# Revit family: SOT_Mavone_Multiproduct_BIM_GB_T0045;T0046;T0047;T0048
name_source: partatom
category: Plumbing Fixtures
revit_build: Autodesk Revit MEP 2014 (Build: 20130308_1515(x64)
units: mm (PartAtom-declared; Revit-internal decimal feet)

## types (16) — shared parameters
Accessories = www.specifysottini.co.uk
AreaUnits = millimeters
Assembly Code = C1030200
AssetType = Fixed
BREEAM = No
Brand = Sottini
CodePerformance = EN 14749:2005
Default Elevation = 900 mm  [stored 2.95276 ft]
DurationUnit = year
ECA = No
ExpectedLife = 30
Finish = White
Handle = SOT_Sottini_Fittings_Chrome_Render
IfcExportAs = IfcFurnitureType
IfcExportType = USERDEFINED
InstallationInstructions = www.idealspec.co.uk/resources.html
LinearUnits = millimeters
MainColor = White
ManufacturerURL = www.specifysottini.co.uk
Material = Laminated board
NBSDescription = Bathroom integrated duct work
NBSReference = 45-35-72/320
NominalDepth = 360 mm
NominalHeight = 400 mm  [stored 1.31234 ft]
NominalLength = 400 mm  [stored 1.31234 ft]
Shape = Rectangular
Space = Internal
SpareParts = www.fastpart-spares.co.uk
SustainabilityPerformance = FSC
TMV3 = No
URL = www.specifysottini.co.uk
Uniclass2 = Pr_40_30_78_04
Version = 1
VolumeUnits = Litres
WRAS = No
WarrantyDescription = Manufacturers warranty
WarrantyDurationParts = 5
WarrantyDurationUnit = year
WaterEfficientProduct = No
zero-valued in all types: CWFU, Cost, HWFU, WFU

## per-type parameters (varying)
| type | BIMObjectName | Color | Description | Features | Laminate | Model | Name | NettWeight | NominalWidth | ProductInformation | Size |
| T0045OV - Mavone 500mm wall hung vanity unit - 1 drawer - Gloss White | SOT_Sottini_Furniture_Mavone_T0045OV | White | Mavone 50 cm wall hung vanity unit with 1 drawer and integrated handle | 50 cm wall hung vanity unit with 1 drawer and integrated handle | SOT_Sottini_Laminate_White_OV_Render | T0045OV | Furniture_Mavone_T0045OV_Sottini | 11 Kg | 500 mm  [stored 1.64042 ft] | www.idealspec.co.uk/assets/datasheet/T0045OV | 360 x 400 x 500 mm |
| T0046OV - Mavone 600mm wall hung vanity unit - 1 drawer - Gloss White | SOT_Sottini_Furniture_Mavone_T0046OV | White | Mavone 60 cm wall hung vanity unit with 1 drawer and integrated handle | 60 cm wall hung vanity unit with 1 drawer and integrated handle | SOT_Sottini_Laminate_White_OV_Render | T0046OV | Furniture_Mavone_T0046OV_Sottini | 14 Kg | 600 mm | www.idealspec.co.uk/assets/datasheet/T0046OV | 360 x 400 x 600 mm |
| T0047OV - Mavone 800mm wall hung vanity unit - 1 drawer - Gloss White | SOT_Sottini_Furniture_Mavone_T0047OV | White | Mavone 80 cm wall hung vanity unit with 1 drawer and integrated handle | 80 cm wall hung vanity unit with 1 drawer and integrated handle | SOT_Sottini_Laminate_White_OV_Render | T0047OV | Furniture_Mavone_T0047OV_Sottini | 18 Kg | 800 mm  [stored 2.62467 ft] | www.idealspec.co.uk/assets/datasheet/T0047OV | 360 x 400 x 800 mm |
| T0048OV - Mavone 1000mm wall hung vanity unit - 1 drawer - Gloss White | SOT_Sottini_Furniture_Mavone_T0048OV | White | Mavone 100 cm wall hung vanity unit with 1 drawer and integrated handle | 100 cm wall hung vanity unit with 1 drawer and integrated handle | SOT_Sottini_Laminate_White_OV_Render | T0048OV | Furniture_Mavone_T0048OV_Sottini | 22 Kg | 1000 mm  [stored 3.28084 ft] | www.idealspec.co.uk/assets/datasheet/T0048OV | 360 x 400 x 1000 mm |
| T0045PH - Mavone 500mm wall hung vanity unit - 1 drawer - Gloss Light Grey | SOT_Sottini_Furniture_Mavone_T0045PH | LightGrey | Mavone 50 cm wall hung vanity unit with 1 drawer and integrated handle | 50 cm wall hung vanity unit with 1 drawer and integrated handle | SOT_Sottini_Laminate_LightGrey_PH_Render | T0045PH | Furniture_Mavone_T0045PH_Sottini | 11 Kg | 500 mm  [stored 1.64042 ft] | www.idealspec.co.uk/assets/datasheet/T0045PH | 360 x 400 x 500 mm |
| T0045PU - Mavone 500mm wall hung vanity unit - 1 drawer - Matt Dark Taupe | SOT_Sottini_Furniture_Mavone_T0045PU | DarkTaupe | Mavone 50 cm wall hung vanity unit with 1 drawer and integrated handle | 50 cm wall hung vanity unit with 1 drawer and integrated handle | SOT_Sottini_Laminate_DarkTaupe_PU_Render | T0045PU | Furniture_Mavone_T0045PU_Sottini | 11 Kg | 500 mm  [stored 1.64042 ft] | www.idealspec.co.uk/assets/datasheet/T0045PU | 360 x 400 x 500 mm |
| T0045VI - Mavone 500mm wall hung vanity unit - 1 drawer - Light Wood | SOT_Sottini_Furniture_Mavone_T0045VI | LightWood | Mavone 50 cm wall hung vanity unit with 1 drawer and integrated handle | 50 cm wall hung vanity unit with 1 drawer and integrated handle | SOT_Sottini_Laminate_LightWood_VI_Render | T0045VI | Furniture_Mavone_T0045VI_Sottini | 11 Kg | 500 mm  [stored 1.64042 ft] | www.idealspec.co.uk/assets/datasheet/T0045VI | 360 x 400 x 500 mm |
| T0046PH - Mavone 600mm wall hung vanity unit - 1 drawer - Gloss Light Grey | SOT_Sottini_Furniture_Mavone_T0046PH | LightGrey | Mavone 60 cm wall hung vanity unit with 1 drawer and integrated handle | 60 cm wall hung vanity unit with 1 drawer and integrated handle | SOT_Sottini_Laminate_LightGrey_PH_Render | T0046PH | Furniture_Mavone_T0046PH_Sottini | 14 Kg | 600 mm | www.idealspec.co.uk/assets/datasheet/T0046PH | 360 x 400 x 600 mm |
| T0046PU - Mavone 600mm wall hung vanity unit - 1 drawer - Matt Dark Taupe | SOT_Sottini_Furniture_Mavone_T0046PU | DarkTaupe | Mavone 60 cm wall hung vanity unit with 1 drawer and integrated handle | 60 cm wall hung vanity unit with 1 drawer and integrated handle | SOT_Sottini_Laminate_DarkTaupe_PU_Render | T0046PU | Furniture_Mavone_T0046PU_Sottini | 14 Kg | 600 mm | www.idealspec.co.uk/assets/datasheet/T0046PU | 360 x 400 x 600 mm |
| T0046VI - Mavone 600mm wall hung vanity unit - 1 drawer - Light Wood | SOT_Sottini_Furniture_Mavone_T0046VI | LightWood | Mavone 60 cm wall hung vanity unit with 1 drawer and integrated handle | 60 cm wall hung vanity unit with 1 drawer and integrated handle | SOT_Sottini_Laminate_LightWood_VI_Render | T0046VI | Furniture_Mavone_T0046VI_Sottini | 14 Kg | 600 mm | www.idealspec.co.uk/assets/datasheet/T0046VI | 360 x 400 x 600 mm |
| T0047PH - Mavone 800mm wall hung vanity unit - 1 drawer - Gloss Light Grey | SOT_Sottini_Furniture_Mavone_T0047PH | LightGrey | Mavone 80 cm wall hung vanity unit with 1 drawer and integrated handle | 80 cm wall hung vanity unit with 1 drawer and integrated handle | SOT_Sottini_Laminate_LightGrey_PH_Render | T0047PH | Furniture_Mavone_T0047PH_Sottini | 18 Kg | 800 mm  [stored 2.62467 ft] | www.idealspec.co.uk/assets/datasheet/T0047PH | 360 x 400 x 800 mm |
| T0047PU - Mavone 800mm wall hung vanity unit - 1 drawer - Matt Dark Taupe | SOT_Sottini_Furniture_Mavone_T0047PU | DarkTaupe | Mavone 80 cm wall hung vanity unit with 1 drawer and integrated handle | 80 cm wall hung vanity unit with 1 drawer and integrated handle | SOT_Sottini_Laminate_DarkTaupe_PU_Render | T0047PU | Furniture_Mavone_T0047PU_Sottini | 18 Kg | 800 mm  [stored 2.62467 ft] | www.idealspec.co.uk/assets/datasheet/T0047PU | 360 x 400 x 800 mm |
| T0047VI - Mavone 800mm wall hung vanity unit - 1 drawer - Light Wood | SOT_Sottini_Furniture_Mavone_T0047VI | LightWood | Mavone 80 cm wall hung vanity unit with 1 drawer and integrated handle | 80 cm wall hung vanity unit with 1 drawer and integrated handle | SOT_Sottini_Laminate_LightWood_VI_Render | T0047VI | Furniture_Mavone_T0047VI_Sottini | 18 Kg | 800 mm  [stored 2.62467 ft] | www.idealspec.co.uk/assets/datasheet/T0047VI | 360 x 400 x 800 mm |
| T0048PH - Mavone 1000mm wall hung vanity unit - 1 drawer - Gloss Light Grey | SOT_Sottini_Furniture_Mavone_T0048PH | LightGrey | Mavone 100 cm wall hung vanity unit with 1 drawer and integrated handle | 100 cm wall hung vanity unit with 1 drawer and integrated handle | SOT_Sottini_Laminate_LightGrey_PH_Render | T0048PH | Furniture_Mavone_T0048PH_Sottini | 22 Kg | 1000 mm  [stored 3.28084 ft] | www.idealspec.co.uk/assets/datasheet/T0048PH | 360 x 400 x 1000 mm |
| T0048PU - Mavone 1000mm wall hung vanity unit - 1 drawer - Matt Dark Taupe | SOT_Sottini_Furniture_Mavone_T0048PU | DarkTaupe | Mavone 100 cm wall hung vanity unit with 1 drawer and integrated handle | 100 cm wall hung vanity unit with 1 drawer and integrated handle | SOT_Sottini_Laminate_DarkTaupe_PU_Render | T0048PU | Furniture_Mavone_T0048PU_Sottini | 22 Kg | 1000 mm  [stored 3.28084 ft] | www.idealspec.co.uk/assets/datasheet/T0048PU | 360 x 400 x 1000 mm |
| T0048VI - Mavone 1000mm wall hung vanity unit - 1 drawer - Light Wood | SOT_Sottini_Furniture_Mavone_T0048VI | LightWood | Mavone 100 cm wall hung vanity unit with 1 drawer and integrated handle | 100 cm wall hung vanity unit with 1 drawer and integrated handle | SOT_Sottini_Laminate_LightWood_VI_Render | T0048VI | Furniture_Mavone_T0048VI_Sottini | 22 Kg | 1000 mm  [stored 3.28084 ft] | www.idealspec.co.uk/assets/datasheet/T0048VI | 360 x 400 x 1000 mm |

note: [stored X ft] marks values corroborated as IEEE doubles in the binary element streams (Revit-internal decimal feet)

## geometry (parser evidence)
native form markers: Sweep x3
no freeform markers — native parametric forms only
